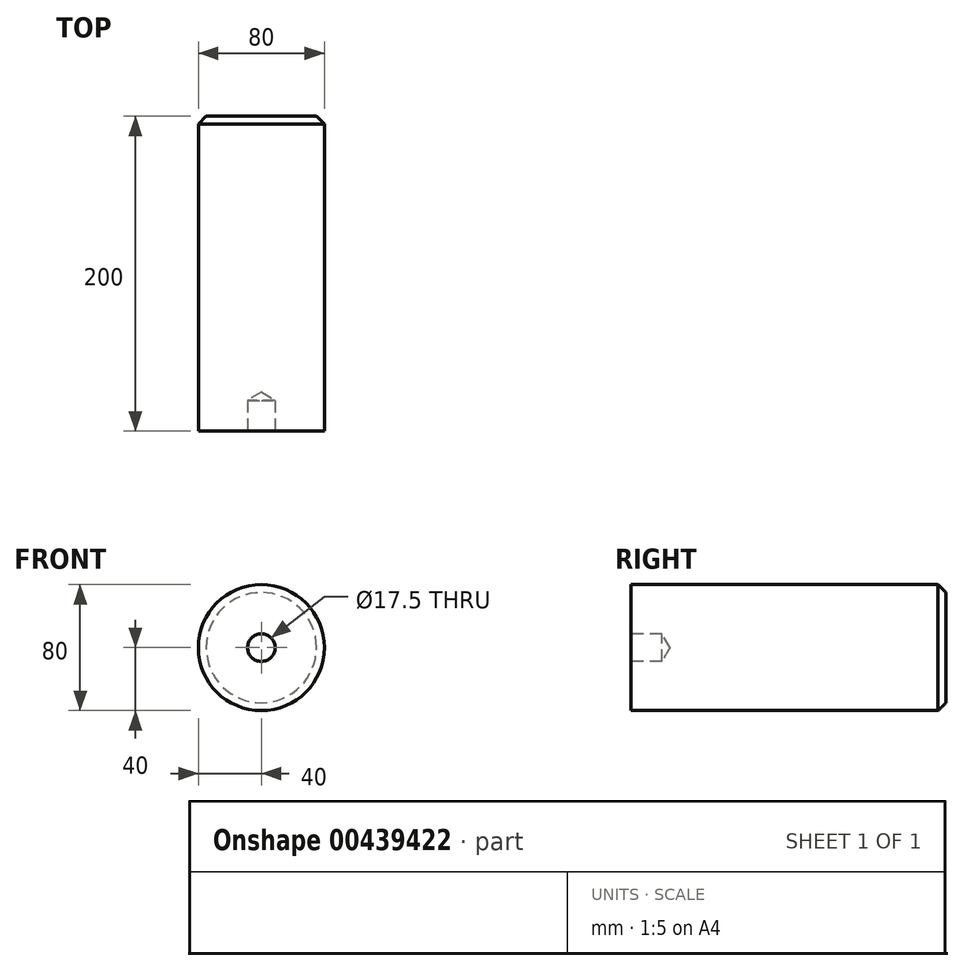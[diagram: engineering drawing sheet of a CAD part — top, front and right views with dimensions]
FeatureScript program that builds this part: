
annotation { "Feature Type Name" : "Feature", "Feature Type Description" : "" }
export const myFeature = defineFeature(function(context is Context, id is Id, definition is map)
    precondition{}
    {
        {
            var Q0;
            Q0=qCreatedBy(makeId("Front.planeOp"),FACE);
            var sketch = newSketch(context, id + "F0", { "sketchPlane" : qUnion([Q0])});
            skCircle(sketch, "E0", {"center": v(0, 0) * mm, "radius": 40 * mm});
            skSolve(sketch);
        }
        {
            var Q0;
            Q0 = qSketchRegion(id + "F0", true);
            extrude(context, id + "F1", {"entities" : qUnion([Q0]), "endBound" : BoundingType.SYMMETRIC, "depth" : 200 * mm});
        }
        {
            var Q0;
            Q0=makeQuery(id+"F1.opExtrude","CAP_EDGE",EDGE,{"disambiguationData":[OSD([sQuery(id+"F0.wireOp",EDGE,"E0")])],"isStart":true});
            chamfer(context, id + "F2", {"entities" : qUnion([Q0]), "width" : 5 * mm, "tangentPropagation" : true});
        }
        {
            var Q0;
            Q0=makeQuery(id+"F1.opExtrude","CAP_FACE",FACE,{"disambiguationData":[OSD([sQuery(id+"F0.wireOp",EDGE,"E0")])],"isStart":false});
            var sketch = newSketch(context, id + "F3", { "sketchPlane" : qUnion([Q0])});
            skPoint(sketch, "E1", {"position": v(0, 0) * mm});
            skSolve(sketch);
        }
        {
            var Q0;
            Q0=sQuery(id+"F3.wireOp",VERTEX,"E1");
            var Q1;
            Q1=makeQuery(id+"F1.opExtrude","SWEPT_BODY",BODY,{"disambiguationData":[OSD([sQuery(id+"F0.wireOp",EDGE,"E0")])]});
            hole(context, id + "F4", {"style" : HoleStyle.SIMPLE, "endStyle" : HoleEndStyle.BLIND, "standardTappedOrClearance" : lookupTablePath({ "standard" : "ISO", "engagement" : "75%", "pitch" : "2.5 mm", "size" : "M20", "type" : "Tapped" }), "standardBlindInLast" : lookupTablePath({ "standard" : "ISO", "engagement" : "75%", "pitch" : "2.5 mm", "size" : "M20", "type" : "Tapped" }), "holeDiameter" : 17.5 * mm, "showTappedDepth" : true, "holeDepth" : 19.5 * mm, "isTappedThrough" : true, "tappedDepth" : 12 * mm, "tapClearance" : 3, "locations" : qUnion([Q0]), "scope" : qUnion([Q1]), "majorDiameter" : 20 * mm});
        }
    });
